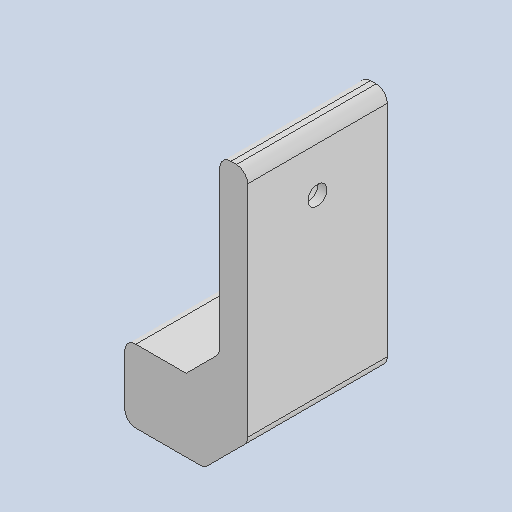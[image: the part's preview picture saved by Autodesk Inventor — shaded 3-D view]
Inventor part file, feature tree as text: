
AUTODESK INVENTOR PART (.ipt)
format: ipt  version: 2022 (Build 260153000, 153)  size: 155,136 bytes
history: native  units: mm
features: other x8, reference x6, sketch x4, extrude x3, chamfer x3, hole x1, fillet x1, projected_geometry x1
ambient origin geometry x8: Origin, YZ Plane, XZ Plane, XY Plane, X Axis, Y Axis, Z Axis, Center Point
bodies: Solid1 (feature_tree)
feature tree (27):
  extrude  "Extrusion1"  Depth=5.0mm
  extrude  "Extrusion2"  Depth=2.0mm
  extrude  "Extrusion3"  Depth=25.0mm
  chamfer  "Chamfer1"  Distance=25.0mm
  chamfer  "Chamfer3"  Distance=3.0mm
  hole  "Hole1"  [1 undecoded]
  fillet  "Fillet3"  Radius=2.0mm
  chamfer  "Chamfer4"  Distance=2.0mm Angle=45.0deg
  sketch  "Sketch1"  dims[d0=5.0mm d1=15.0mm]
  sketch  "Sketch2"  dims[d2=4.0mm d3=2.0mm]
  reference  "Reference1"
  reference  "Reference2"
  sketch  "Sketch3"  dims[d4=40.85mm d5=6.0mm d6=25.0mm d7=0.0mm]
  projected_geometry  "Projected Loop1"
  reference  "Reference3"
  reference  "Reference4"
  reference  "Reference5"
  sketch  "Sketch5"  dims[d8=7.0mm d9=3.0mm d10=0.0mm d13=3.0mm d14=0.0mm d16=7.75mm d17=2.0mm d18=45.0deg d24=6.0mm d25=2.0mm d26=45.0deg d27=3.4mm d28=6.0mm d29=6.5mm d30=3.4mm d31=90.0deg d32=8.0mm d33=20.594885mm d34=2.0mm d35=2.0mm d36=2.0mm d37=45.0deg d38=7.0mm]
  reference  "Reference6"
  parser-record x1  (decoder bookkeeping rows leaked as tree rows — omitted from the tree; the rows remain in map.json)
  other  "Bibble0.iam"
  other  "603 Bearing:10"
  other  "603 Bearing:14"
  other  "603 Bearing:15"
  other  "2020 Y Axis:5"
  other  "603 Bearing:12"
  other  "2020 X Axis:3"
note: 1 required parameter value undecoded (feature->parameter linkage not recoverable at this tier; creation-order binding heuristic only, values carry confidence <= 0.55)
note: 1 file-system path scrubbed to <path> (originals preserved in map.json)
